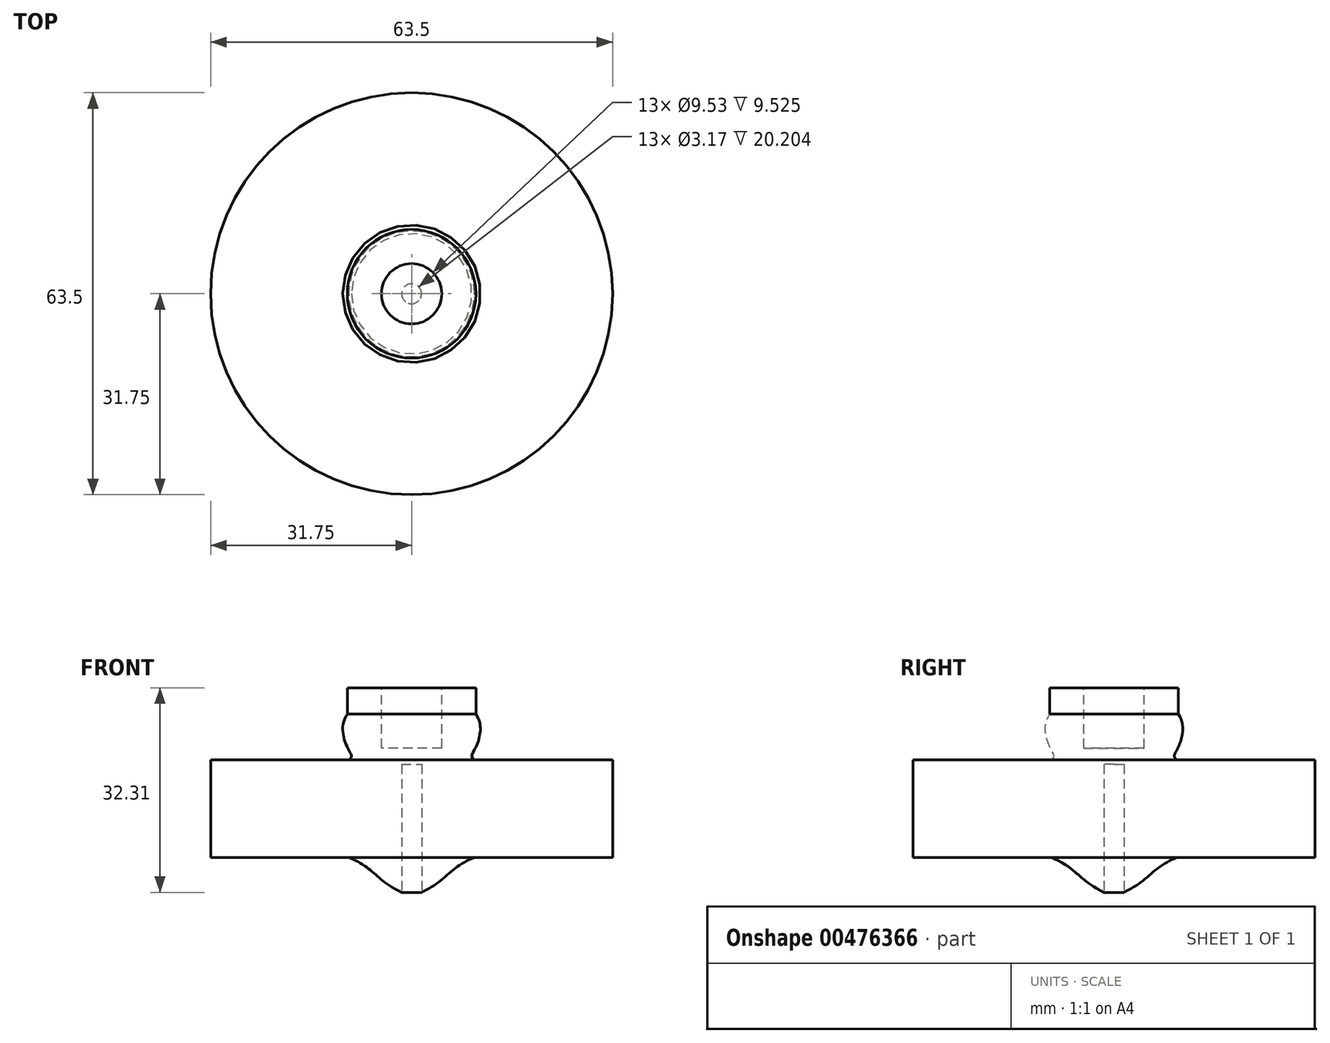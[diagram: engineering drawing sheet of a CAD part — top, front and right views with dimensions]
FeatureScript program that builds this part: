
annotation { "Feature Type Name" : "Feature", "Feature Type Description" : "" }
export const myFeature = defineFeature(function(context is Context, id is Id, definition is map)
    precondition{}
    {
        {
            var Q0;
            Q0=qCreatedBy(makeId("Front.planeOp"),FACE);
            var sketch = newSketch(context, id + "F0", { "sketchPlane" : qUnion([Q0])});
            skLineSegment(sketch, "E0", {"start": v(0, 0) * mm, "end": v(0, 33.02) * mm});
            skFitSpline(sketch, "E1", {"points": [v(0, 33.02) * mm, v(10.16, 28.86) * mm, v(9.91, 23.19) * mm, v(9.91, 21.64) * mm, v(31.75, 13.93) * mm, v(9.91, 6.21) * mm, v(0, 0) * mm], "startDerivative": vector(36.31, 3.17) * mm, "endDerivative": vector(-103.93, -42.74) * mm});
            skLineSegment(sketch, "E2", {"start": v(0, 33.02) * mm, "end": v(10.16, 33.02) * mm});
            skLineSegment(sketch, "E3", {"start": v(10.16, 33.02) * mm, "end": v(10.16, 28.86) * mm});
            skLineSegment(sketch, "E4", {"start": v(9.91, 21.64) * mm, "end": v(9.91, 6.21) * mm});
            skLineSegment(sketch, "E5", {"start": v(9.91, 13.93) * mm, "end": v(31.75, 13.93) * mm});
            skLineSegment(sketch, "E6", {"start": v(31.75, 13.93) * mm, "end": v(31.75, 21.64) * mm});
            skLineSegment(sketch, "E7", {"start": v(9.91, 21.64) * mm, "end": v(31.75, 21.64) * mm});
            skLineSegment(sketch, "E8", {"start": v(9.91, 6.21) * mm, "end": v(31.75, 6.21) * mm});
            skLineSegment(sketch, "E9", {"start": v(31.75, 6.21) * mm, "end": v(31.75, 13.93) * mm});
            skLineSegment(sketch, "E10", {"start": v(0, 0) * mm, "end": v(31.75, 0) * mm});
            skSolve(sketch);
        }
        {
            var Q0;
            Q0=makeQuery(id+"F0.imprint","IMPRINT",FACE,{"disambiguationData":[TD([[makeQuery(id+"F0.imprint","IMPRINT",EDGE,{"derivedFrom":sQuery(id+"F0.wireOp",EDGE,"E0")}),-1.0]])]});
            var Q1;
            {var subQ0=sQuery(id+"F0.wireOp",EDGE,"E3");Q1=makeQuery(id+"F0.imprint","IMPRINT",FACE,{"disambiguationData":[TD([[makeQuery(id+"F0.imprint","IMPRINT",EDGE,{"derivedFrom":subQ0}),-1.0]])]});}
            var Q2;
            {var subQ3=sQuery(id+"F0.wireOp",EDGE,"E5");Q2=makeQuery(id+"F0.imprint","IMPRINT",FACE,{"disambiguationData":[TD([[makeQuery(id+"F0.imprint","IMPRINT",EDGE,{"derivedFrom":subQ3}),-1.0]])]});}
            var Q3;
            {var subQ3=sQuery(id+"F0.wireOp",EDGE,"E5");Q3=makeQuery(id+"F0.imprint","IMPRINT",FACE,{"disambiguationData":[TD([[makeQuery(id+"F0.imprint","IMPRINT",EDGE,{"derivedFrom":subQ3}),1.0]])]});}
            var Q4;
            {var subQ2=sQuery(id+"F0.wireOp",EDGE,"E6");Q4=makeQuery(id+"F0.imprint","IMPRINT",FACE,{"disambiguationData":[TD([[makeQuery(id+"F0.imprint","IMPRINT",EDGE,{"derivedFrom":subQ2}),1.0]])]});}
            var Q5;
            {var subQ0=sQuery(id+"F0.wireOp",EDGE,"E8");Q5=makeQuery(id+"F0.imprint","IMPRINT",FACE,{"disambiguationData":[TD([[makeQuery(id+"F0.imprint","IMPRINT",EDGE,{"derivedFrom":subQ0}),1.0]])]});}
            var Q6;
            Q6=sQuery(id+"F0.wireOp",EDGE,"E0");
            revolve(context, id + "F1", {"entities" : qUnion([Q0, Q1, Q2, Q3, Q4, Q5]), "axis" : qUnion([Q6]), "revolveType" : RevolveType.FULL});
        }
        {
            var Q0;
            Q0=makeQuery(id+"F1.opRevolve","SWEPT_FACE",FACE,{"disambiguationData":[OSD([sQuery(id+"F0.wireOp",EDGE,"E2")])]});
            var sketch = newSketch(context, id + "F2", { "sketchPlane" : qUnion([Q0])});
            skCircle(sketch, "E11", {"center": v(0, 0) * mm, "radius": 4.76 * mm});
            skSolve(sketch);
        }
        {
            var Q0;
            Q0=makeQuery(id+"F2.imprint","IMPRINT",FACE,{"disambiguationData":[TD([[makeQuery(id+"F2.imprint","IMPRINT",EDGE,{"derivedFrom":sQuery(id+"F2.wireOp",EDGE,"E11")}),1.0]])]});
            extrude(context, id + "F3", {"entities" : qUnion([Q0]), "operationType" : NewBodyOperationType.REMOVE, "oppositeDirection" : true, "depth" : 9.52 * mm});
        }
        {
            var Q0;
            Q0=qCreatedBy(makeId("Top.planeOp"),FACE);
            var sketch = newSketch(context, id + "F4", { "sketchPlane" : qUnion([Q0])});
            skCircle(sketch, "E12", {"center": v(0, 0) * mm, "radius": 1.59 * mm});
            skSolve(sketch);
        }
        {
            var Q0;
            Q0=makeQuery(id+"F4.imprint","IMPRINT",FACE,{"disambiguationData":[TD([[makeQuery(id+"F4.imprint","IMPRINT",EDGE,{"derivedFrom":sQuery(id+"F4.wireOp",EDGE,"E12")}),1.0]])]});
            extrude(context, id + "F5", {"entities" : qUnion([Q0]), "operationType" : NewBodyOperationType.REMOVE, "depth" : 20.92 * mm});
        }
    });
